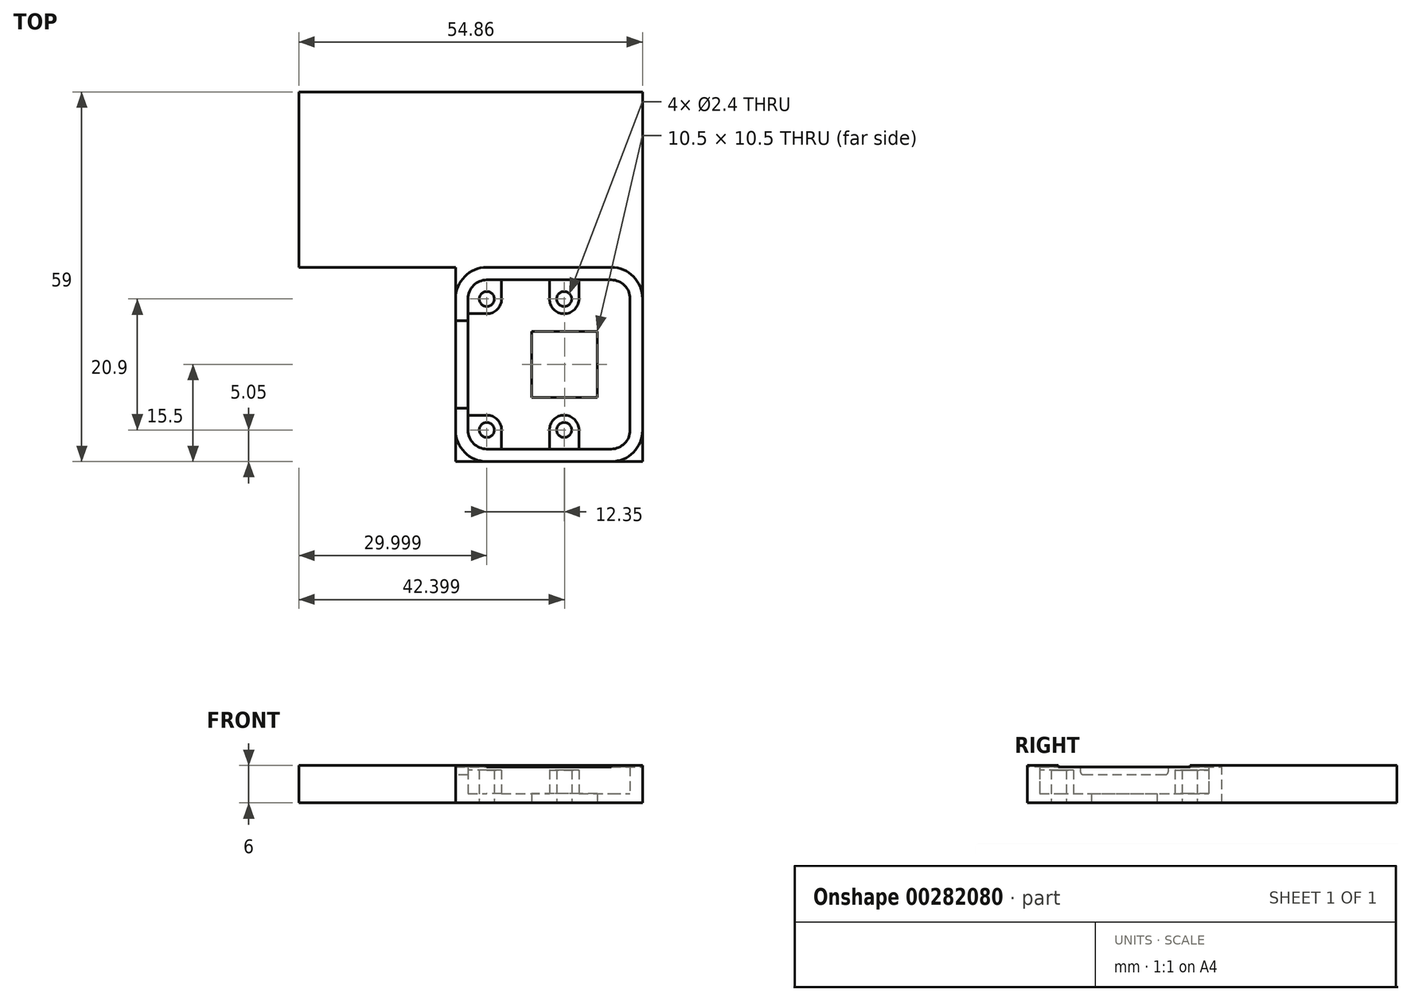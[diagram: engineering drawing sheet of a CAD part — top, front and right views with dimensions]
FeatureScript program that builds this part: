
annotation { "Feature Type Name" : "Feature", "Feature Type Description" : "" }
export const myFeature = defineFeature(function(context is Context, id is Id, definition is map)
    precondition{}
    {
        {
            var Q0;
            Q0=qCreatedBy(makeId("Top.planeOp"),FACE);
            var sketch = newSketch(context, id + "F0", { "sketchPlane" : qUnion([Q0])});
            skPoint(sketch, "E0.middle", {"position": v(0, 0) * mm});
            skPoint(sketch, "E1.visualSharp", {"position": v(-11.93, 12.5) * mm});
            skPoint(sketch, "E2.visualSharp", {"position": v(-11.93, -12.5) * mm});
            skPoint(sketch, "E3.visualSharp", {"position": v(11.93, 12.5) * mm});
            skPoint(sketch, "E4.visualSharp", {"position": v(11.93, -12.5) * mm});
            skLineSegment(sketch, "E5", {"start": v(-9.93, 14.98) * mm, "end": v(-9.93, -15.05) * mm, "construction": true});
            skLineSegment(sketch, "E6", {"start": v(-20.4, -10.45) * mm, "end": v(21.47, -10.45) * mm, "construction": true});
            skLineSegment(sketch, "E7", {"start": v(-14.71, 10.45) * mm, "end": v(19.25, 10.45) * mm, "construction": true});
            skCircle(sketch, "E8", {"center": v(-9.93, 10.45) * mm, "radius": 1.2 * mm});
            skCircle(sketch, "E9", {"center": v(-9.93, -10.45) * mm, "radius": 1.2 * mm});
            skLineSegment(sketch, "E10", {"start": v(2.42, 14.76) * mm, "end": v(2.42, -15.1) * mm, "construction": true});
            skCircle(sketch, "E11", {"center": v(2.42, 10.45) * mm, "radius": 1.2 * mm});
            skCircle(sketch, "E12", {"center": v(2.42, -10.45) * mm, "radius": 1.2 * mm});
            skLineSegment(sketch, "E13", {"start": v(2.47, 15.16) * mm, "end": v(2.47, -14.75) * mm, "construction": true});
            skLineSegment(sketch, "E14.bottom", {"start": v(6.72, -4.25) * mm, "end": v(-1.78, -4.25) * mm});
            skLineSegment(sketch, "E14.top", {"start": v(6.72, 4.25) * mm, "end": v(-1.78, 4.25) * mm});
            skLineSegment(sketch, "E14.left", {"start": v(6.72, -4.25) * mm, "end": v(6.72, 4.25) * mm});
            skLineSegment(sketch, "E14.right", {"start": v(-1.78, -4.25) * mm, "end": v(-1.78, 4.25) * mm});
            skPoint(sketch, "E14.middle", {"position": v(2.47, 0) * mm});
            skCircle(sketch, "E15", {"center": v(-9.93, 10.45) * mm, "radius": 2.35 * mm});
            skCircle(sketch, "E16", {"center": v(-9.93, -10.45) * mm, "radius": 2.35 * mm});
            skCircle(sketch, "E17", {"center": v(2.42, -10.45) * mm, "radius": 2.35 * mm});
            skCircle(sketch, "E18", {"center": v(2.42, 10.45) * mm, "radius": 2.35 * mm});
            skLineSegment(sketch, "E19.0", {"start": v(7.72, 5.25) * mm, "end": v(-2.78, 5.25) * mm});
            skLineSegment(sketch, "E19.1", {"start": v(7.72, -5.25) * mm, "end": v(7.72, 5.25) * mm});
            skLineSegment(sketch, "E19.2", {"start": v(7.72, -5.25) * mm, "end": v(-2.78, -5.25) * mm});
            skLineSegment(sketch, "E19.3", {"start": v(-2.78, -5.25) * mm, "end": v(-2.78, 5.25) * mm});
            skLineSegment(sketch, "E20.0", {"start": v(9.93, 13.5) * mm, "end": v(-9.93, 13.5) * mm});
            skArc(sketch, "E20.1", {"start": v(12.93, 10.5) * mm, "mid": v(12.05, 12.62) * mm, "end": v(9.93, 13.5) * mm});
            skArc(sketch, "E20.2", {"start": v(-9.93, 13.5) * mm, "mid": v(-12.05, 12.62) * mm, "end": v(-12.93, 10.5) * mm});
            skLineSegment(sketch, "E20.3", {"start": v(12.93, 10.5) * mm, "end": v(12.93, -10.5) * mm});
            skLineSegment(sketch, "E20.4", {"start": v(-12.93, 10.5) * mm, "end": v(-12.93, -10.5) * mm});
            skArc(sketch, "E20.5", {"start": v(-12.93, -10.5) * mm, "mid": v(-12.05, -12.62) * mm, "end": v(-9.93, -13.5) * mm});
            skLineSegment(sketch, "E20.6", {"start": v(9.93, -13.5) * mm, "end": v(-9.93, -13.5) * mm});
            skArc(sketch, "E20.7", {"start": v(9.93, -13.5) * mm, "mid": v(12.05, -12.62) * mm, "end": v(12.93, -10.5) * mm});
            skArc(sketch, "E21.0", {"start": v(14.93, 10.5) * mm, "mid": v(13.47, 14.04) * mm, "end": v(9.93, 15.5) * mm});
            skLineSegment(sketch, "E21.1", {"start": v(14.93, 10.5) * mm, "end": v(14.93, -10.5) * mm});
            skLineSegment(sketch, "E21.2", {"start": v(9.93, 15.5) * mm, "end": v(-9.93, 15.5) * mm});
            skArc(sketch, "E21.3", {"start": v(9.93, -15.5) * mm, "mid": v(13.47, -14.04) * mm, "end": v(14.93, -10.5) * mm});
            skArc(sketch, "E21.4", {"start": v(-9.93, 15.5) * mm, "mid": v(-13.47, 14.04) * mm, "end": v(-14.93, 10.5) * mm});
            skLineSegment(sketch, "E21.5", {"start": v(-14.93, 10.5) * mm, "end": v(-14.93, -10.5) * mm});
            skArc(sketch, "E21.6", {"start": v(-14.93, -10.5) * mm, "mid": v(-13.47, -14.04) * mm, "end": v(-9.93, -15.5) * mm});
            skLineSegment(sketch, "E21.7", {"start": v(9.93, -15.5) * mm, "end": v(-9.93, -15.5) * mm});
            skLineSegment(sketch, "E22", {"start": v(-9.93, 8.1) * mm, "end": v(-12.93, 8.1) * mm});
            skLineSegment(sketch, "E23", {"start": v(-7.58, 10.45) * mm, "end": v(-7.58, 13.5) * mm});
            skLineSegment(sketch, "E24", {"start": v(0.07, 10.45) * mm, "end": v(0.07, 13.5) * mm});
            skLineSegment(sketch, "E25", {"start": v(4.77, 10.45) * mm, "end": v(4.77, 13.5) * mm});
            skLineSegment(sketch, "E26", {"start": v(0.07, -10.45) * mm, "end": v(0.07, -13.5) * mm});
            skLineSegment(sketch, "E27", {"start": v(4.77, -10.45) * mm, "end": v(4.77, -13.5) * mm});
            skLineSegment(sketch, "E28", {"start": v(-9.93, -8.1) * mm, "end": v(-12.93, -8.1) * mm});
            skLineSegment(sketch, "E29", {"start": v(-7.58, -10.45) * mm, "end": v(-7.58, -13.5) * mm});
            skLineSegment(sketch, "E30", {"start": v(14.93, 10.5) * mm, "end": v(14.93, 14.98) * mm});
            skLineSegment(sketch, "E31", {"start": v(9.93, 15.5) * mm, "end": v(14.93, 15.5) * mm});
            skLineSegment(sketch, "E32", {"start": v(14.93, 15.5) * mm, "end": v(14.93, 14.98) * mm});
            skLineSegment(sketch, "E33", {"start": v(9.93, -15.5) * mm, "end": v(14.93, -15.5) * mm});
            skLineSegment(sketch, "E34", {"start": v(14.93, -15.5) * mm, "end": v(14.93, -10.5) * mm});
            skLineSegment(sketch, "E35", {"start": v(-14.93, 10.5) * mm, "end": v(-14.93, 15.5) * mm});
            skLineSegment(sketch, "E36", {"start": v(-14.93, 15.5) * mm, "end": v(-9.93, 15.5) * mm});
            skLineSegment(sketch, "E37", {"start": v(-14.93, -10.5) * mm, "end": v(-14.93, -15.5) * mm});
            skLineSegment(sketch, "E38", {"start": v(-14.93, -15.5) * mm, "end": v(-9.93, -15.5) * mm});
            skLineSegment(sketch, "E39.left", {"start": v(-14.93, 15.5) * mm, "end": v(-14.93, -15.5) * mm});
            skLineSegment(sketch, "E40.left", {"start": v(14.93, 15.5) * mm, "end": v(14.93, -15.5) * mm});
            skLineSegment(sketch, "E41", {"start": v(-14.93, 15.5) * mm, "end": v(-14.93, 43.5) * mm});
            skLineSegment(sketch, "E42", {"start": v(-14.93, 43.5) * mm, "end": v(14.93, 43.5) * mm});
            skLineSegment(sketch, "E43", {"start": v(14.93, 43.5) * mm, "end": v(14.93, 15.5) * mm});
            skLineSegment(sketch, "E44", {"start": v(-14.93, 15.5) * mm, "end": v(-39.93, 15.5) * mm});
            skLineSegment(sketch, "E45", {"start": v(-39.93, 15.5) * mm, "end": v(-39.93, 43.5) * mm});
            skLineSegment(sketch, "E46", {"start": v(-39.93, 43.5) * mm, "end": v(-14.93, 43.5) * mm});
            skSolve(sketch);
        }
        {
            var Q0;
            Q0=makeQuery(id+"F0.imprint","IMPRINT",FACE,{"disambiguationData":[TD([[makeQuery(id+"F0.imprint","IMPRINT",EDGE,{"derivedFrom":sQuery(id+"F0.wireOp",EDGE,"E20.0")}),-1.0]])]});
            var Q1;
            Q1=makeQuery(id+"F0.imprint","IMPRINT",FACE,{"disambiguationData":[TD([[makeQuery(id+"F0.imprint","IMPRINT",EDGE,{"derivedFrom":sQuery(id+"F0.wireOp",EDGE,"E0.left")}),-1.0]])]});
            var Q2;
            Q2=makeQuery(id+"F0.imprint","IMPRINT",FACE,{"disambiguationData":[TD([[makeQuery(id+"F0.imprint","IMPRINT",EDGE,{"derivedFrom":sQuery(id+"F0.wireOp",EDGE,"E12")}),-1.0]])]});
            var Q3;
            {var subQ0=sQuery(id+"F0.wireOp",EDGE,"E2.filletArc");Q3=makeQuery(id+"F0.imprint","IMPRINT",FACE,{"disambiguationData":[TD([[makeQuery(id+"F0.imprint","IMPRINT",EDGE,{"derivedFrom":subQ0}),1.0]])]});}
            var Q4;
            Q4=makeQuery(id+"F0.imprint","IMPRINT",FACE,{"disambiguationData":[TD([[makeQuery(id+"F0.imprint","IMPRINT",EDGE,{"derivedFrom":sQuery(id+"F0.wireOp",EDGE,"E0.left")}),1.0]])]});
            var Q5;
            {var subQ0=sQuery(id+"F0.wireOp",EDGE,"E1.filletArc");Q5=makeQuery(id+"F0.imprint","IMPRINT",FACE,{"disambiguationData":[TD([[makeQuery(id+"F0.imprint","IMPRINT",EDGE,{"derivedFrom":subQ0}),1.0]])]});}
            var Q6;
            Q6=makeQuery(id+"F0.imprint","IMPRINT",FACE,{"disambiguationData":[TD([[makeQuery(id+"F0.imprint","IMPRINT",EDGE,{"derivedFrom":sQuery(id+"F0.wireOp",EDGE,"E11")}),-1.0]])]});
            var Q7;
            {var subQ0=sQuery(id+"F0.wireOp",EDGE,"E18");var subQ1=sQuery(id+"F0.wireOp",EDGE,"E0.bottom");var subQ2=makeQuery(id+"F0.imprint","INTERSECT",VERTEX,{"disambiguationData":[OD(0.0)],"derivedFrom":[subQ1,subQ0]});Q7=makeQuery(id+"F0.imprint","IMPRINT",FACE,{"disambiguationData":[TD([[makeQuery(id+"F0.imprint","IMPRINT",EDGE,{"disambiguationData":[TD([[subQ2,-1.0]])],"derivedFrom":subQ1}),-1.0]])]});}
            var Q8;
            {var subQ0=sQuery(id+"F0.wireOp",EDGE,"E1.filletArc");Q8=makeQuery(id+"F0.imprint","IMPRINT",FACE,{"disambiguationData":[TD([[makeQuery(id+"F0.imprint","IMPRINT",EDGE,{"derivedFrom":subQ0}),-1.0]])]});}
            var Q9;
            {var subQ0=sQuery(id+"F0.wireOp",EDGE,"E2.filletArc");Q9=makeQuery(id+"F0.imprint","IMPRINT",FACE,{"disambiguationData":[TD([[makeQuery(id+"F0.imprint","IMPRINT",EDGE,{"derivedFrom":subQ0}),-1.0]])]});}
            var Q10;
            {var subQ0=sQuery(id+"F0.wireOp",EDGE,"E17");var subQ1=sQuery(id+"F0.wireOp",EDGE,"E0.top");var subQ2=makeQuery(id+"F0.imprint","INTERSECT",VERTEX,{"disambiguationData":[OD(0.0)],"derivedFrom":[subQ1,subQ0]});Q10=makeQuery(id+"F0.imprint","IMPRINT",FACE,{"disambiguationData":[TD([[makeQuery(id+"F0.imprint","IMPRINT",EDGE,{"disambiguationData":[TD([[subQ2,-1.0]])],"derivedFrom":subQ1}),1.0]])]});}
            var Q11;
            {var subQ0=sQuery(id+"F0.wireOp",EDGE,"E20.2");Q11=makeQuery(id+"F0.imprint","IMPRINT",FACE,{"disambiguationData":[TD([[makeQuery(id+"F0.imprint","IMPRINT",EDGE,{"derivedFrom":subQ0}),1.0]])]});}
            var Q12;
            {var subQ0=sQuery(id+"F0.wireOp",EDGE,"E22");var subQ1=sQuery(id+"F0.wireOp",EDGE,"E0.right");var subQ2=makeQuery(id+"F0.imprint","INTERSECT",VERTEX,{"derivedFrom":[subQ1,subQ0]});Q12=makeQuery(id+"F0.imprint","IMPRINT",FACE,{"disambiguationData":[TD([[makeQuery(id+"F0.imprint","IMPRINT",EDGE,{"disambiguationData":[TD([[subQ2,-1.0]])],"derivedFrom":subQ1}),-1.0]])]});}
            var Q13;
            {var subQ0=sQuery(id+"F0.wireOp",EDGE,"E20.5");Q13=makeQuery(id+"F0.imprint","IMPRINT",FACE,{"disambiguationData":[TD([[makeQuery(id+"F0.imprint","IMPRINT",EDGE,{"derivedFrom":subQ0}),1.0]])]});}
            var Q14;
            {var subQ0=sQuery(id+"F0.wireOp",EDGE,"E28");var subQ1=sQuery(id+"F0.wireOp",EDGE,"E0.right");var subQ2=makeQuery(id+"F0.imprint","INTERSECT",VERTEX,{"derivedFrom":[subQ1,subQ0]});Q14=makeQuery(id+"F0.imprint","IMPRINT",FACE,{"disambiguationData":[TD([[makeQuery(id+"F0.imprint","IMPRINT",EDGE,{"disambiguationData":[TD([[subQ2,-1.0]])],"derivedFrom":subQ1}),1.0]])]});}
            var Q15;
            {var subQ0=sQuery(id+"F0.wireOp",EDGE,"E29");var subQ1=sQuery(id+"F0.wireOp",EDGE,"E0.top");var subQ2=makeQuery(id+"F0.imprint","INTERSECT",VERTEX,{"derivedFrom":[subQ1,subQ0]});Q15=makeQuery(id+"F0.imprint","IMPRINT",FACE,{"disambiguationData":[TD([[makeQuery(id+"F0.imprint","IMPRINT",EDGE,{"disambiguationData":[TD([[subQ2,-1.0]])],"derivedFrom":subQ1}),-1.0]])]});}
            var Q16;
            {var subQ0=sQuery(id+"F0.wireOp",EDGE,"E26");var subQ1=sQuery(id+"F0.wireOp",EDGE,"E0.top");var subQ2=makeQuery(id+"F0.imprint","INTERSECT",VERTEX,{"derivedFrom":[subQ1,subQ0]});Q16=makeQuery(id+"F0.imprint","IMPRINT",FACE,{"disambiguationData":[TD([[makeQuery(id+"F0.imprint","IMPRINT",EDGE,{"disambiguationData":[TD([[subQ2,-1.0]])],"derivedFrom":subQ1}),1.0]])]});}
            var Q17;
            {var subQ3=sQuery(id+"F0.wireOp",EDGE,"E27");var subQ6=sQuery(id+"F0.wireOp",EDGE,"E0.top");var subQ10=makeQuery(id+"F0.imprint","INTERSECT",VERTEX,{"derivedFrom":[subQ6,subQ3]});Q17=makeQuery(id+"F0.imprint","IMPRINT",FACE,{"disambiguationData":[TD([[makeQuery(id+"F0.imprint","IMPRINT",EDGE,{"disambiguationData":[TD([[subQ10,-1.0]])],"derivedFrom":subQ6}),1.0]])]});}
            var Q18;
            {var subQ0=sQuery(id+"F0.wireOp",EDGE,"E27");var subQ1=sQuery(id+"F0.wireOp",EDGE,"E0.top");var subQ2=makeQuery(id+"F0.imprint","INTERSECT",VERTEX,{"derivedFrom":[subQ1,subQ0]});Q18=makeQuery(id+"F0.imprint","IMPRINT",FACE,{"disambiguationData":[TD([[makeQuery(id+"F0.imprint","IMPRINT",EDGE,{"disambiguationData":[TD([[subQ2,-1.0]])],"derivedFrom":subQ1}),-1.0]])]});}
            var Q19;
            {var subQ0=sQuery(id+"F0.wireOp",EDGE,"E17");var subQ1=sQuery(id+"F0.wireOp",EDGE,"E0.top");var subQ2=makeQuery(id+"F0.imprint","INTERSECT",VERTEX,{"disambiguationData":[OD(1.0)],"derivedFrom":[subQ1,subQ0]});Q19=makeQuery(id+"F0.imprint","IMPRINT",FACE,{"disambiguationData":[TD([[makeQuery(id+"F0.imprint","IMPRINT",EDGE,{"disambiguationData":[TD([[subQ2,-1.0]])],"derivedFrom":subQ1}),-1.0]])]});}
            var Q20;
            {var subQ0=sQuery(id+"F0.wireOp",EDGE,"E23");var subQ1=sQuery(id+"F0.wireOp",EDGE,"E0.bottom");var subQ2=makeQuery(id+"F0.imprint","INTERSECT",VERTEX,{"derivedFrom":[subQ1,subQ0]});Q20=makeQuery(id+"F0.imprint","IMPRINT",FACE,{"disambiguationData":[TD([[makeQuery(id+"F0.imprint","IMPRINT",EDGE,{"disambiguationData":[TD([[subQ2,-1.0]])],"derivedFrom":subQ1}),1.0]])]});}
            var Q21;
            {var subQ0=sQuery(id+"F0.wireOp",EDGE,"E15");var subQ1=sQuery(id+"F0.wireOp",EDGE,"E0.right");var subQ2=makeQuery(id+"F0.imprint","INTERSECT",VERTEX,{"derivedFrom":[subQ1,subQ0]});Q21=makeQuery(id+"F0.imprint","IMPRINT",FACE,{"disambiguationData":[TD([[makeQuery(id+"F0.imprint","IMPRINT",EDGE,{"disambiguationData":[TD([[subQ2,-1.0]])],"derivedFrom":subQ1}),1.0]])]});}
            var Q22;
            {var subQ0=sQuery(id+"F0.wireOp",EDGE,"E24");var subQ1=sQuery(id+"F0.wireOp",EDGE,"E0.bottom");var subQ2=makeQuery(id+"F0.imprint","INTERSECT",VERTEX,{"derivedFrom":[subQ1,subQ0]});Q22=makeQuery(id+"F0.imprint","IMPRINT",FACE,{"disambiguationData":[TD([[makeQuery(id+"F0.imprint","IMPRINT",EDGE,{"disambiguationData":[TD([[subQ2,-1.0]])],"derivedFrom":subQ1}),-1.0]])]});}
            var Q23;
            {var subQ0=sQuery(id+"F0.wireOp",EDGE,"E18");var subQ1=sQuery(id+"F0.wireOp",EDGE,"E0.bottom");var subQ2=makeQuery(id+"F0.imprint","INTERSECT",VERTEX,{"disambiguationData":[OD(1.0)],"derivedFrom":[subQ1,subQ0]});Q23=makeQuery(id+"F0.imprint","IMPRINT",FACE,{"disambiguationData":[TD([[makeQuery(id+"F0.imprint","IMPRINT",EDGE,{"disambiguationData":[TD([[subQ2,-1.0]])],"derivedFrom":subQ1}),1.0]])]});}
            var Q24;
            {var subQ1=sQuery(id+"F0.wireOp",EDGE,"E0.bottom");var subQ7=sQuery(id+"F0.wireOp",EDGE,"E25");var subQ9=makeQuery(id+"F0.imprint","INTERSECT",VERTEX,{"derivedFrom":[subQ1,subQ7]});Q24=makeQuery(id+"F0.imprint","IMPRINT",FACE,{"disambiguationData":[TD([[makeQuery(id+"F0.imprint","IMPRINT",EDGE,{"disambiguationData":[TD([[subQ9,-1.0]])],"derivedFrom":subQ1}),-1.0]])]});}
            var Q25;
            {var subQ0=sQuery(id+"F0.wireOp",EDGE,"E25");var subQ1=sQuery(id+"F0.wireOp",EDGE,"E0.bottom");var subQ2=makeQuery(id+"F0.imprint","INTERSECT",VERTEX,{"derivedFrom":[subQ1,subQ0]});Q25=makeQuery(id+"F0.imprint","IMPRINT",FACE,{"disambiguationData":[TD([[makeQuery(id+"F0.imprint","IMPRINT",EDGE,{"disambiguationData":[TD([[subQ2,-1.0]])],"derivedFrom":subQ1}),1.0]])]});}
            var Q26;
            Q26=makeQuery(id+"F0.imprint","IMPRINT",FACE,{"disambiguationData":[TD([[makeQuery(id+"F0.imprint","IMPRINT",EDGE,{"derivedFrom":sQuery(id+"F0.wireOp",EDGE,"E19.0")}),-1.0]])]});
            var Q27;
            Q27=makeQuery(id+"F0.imprint","IMPRINT",FACE,{"disambiguationData":[TD([[makeQuery(id+"F0.imprint","IMPRINT",EDGE,{"derivedFrom":sQuery(id+"F0.wireOp",EDGE,"E9")}),-1.0]])]});
            var Q28;
            {var subQ0=sQuery(id+"F0.wireOp",EDGE,"E26");Q28=makeQuery(id+"F0.imprint","IMPRINT",FACE,{"disambiguationData":[TD([[makeQuery(id+"F0.imprint","IMPRINT",EDGE,{"derivedFrom":subQ0}),1.0]])]});}
            var Q29;
            Q29=makeQuery(id+"F0.imprint","IMPRINT",FACE,{"disambiguationData":[TD([[makeQuery(id+"F0.imprint","IMPRINT",EDGE,{"derivedFrom":sQuery(id+"F0.wireOp",EDGE,"E8")}),-1.0]])]});
            var Q30;
            {var subQ0=sQuery(id+"F0.wireOp",EDGE,"E24");Q30=makeQuery(id+"F0.imprint","IMPRINT",FACE,{"disambiguationData":[TD([[makeQuery(id+"F0.imprint","IMPRINT",EDGE,{"derivedFrom":subQ0}),-1.0]])]});}
            extrude(context, id + "F1", {"entities" : qUnion([Q0, Q1, Q2, Q3, Q4, Q5, Q6, Q7, Q8, Q9, Q10, Q11, Q12, Q13, Q14, Q15, Q16, Q17, Q18, Q19, Q20, Q21, Q22, Q23, Q24, Q25, Q26, Q27, Q28, Q29, Q30]), "depth" : 1.5 * mm});
        }
        {
            var Q0;
            {var subQ1=sQuery(id+"F0.wireOp",EDGE,"E20.2");Q0=makeQuery(id+"F0.imprint","IMPRINT",FACE,{"disambiguationData":[TD([[makeQuery(id+"F0.imprint","IMPRINT",EDGE,{"derivedFrom":subQ1}),1.0]])]});}
            var Q1;
            Q1=makeQuery(id+"F0.imprint","IMPRINT",FACE,{"disambiguationData":[TD([[makeQuery(id+"F0.imprint","IMPRINT",EDGE,{"derivedFrom":sQuery(id+"F0.wireOp",EDGE,"E8")}),-1.0]])]});
            var Q2;
            Q2=makeQuery(id+"F0.imprint","IMPRINT",FACE,{"disambiguationData":[TD([[makeQuery(id+"F0.imprint","IMPRINT",EDGE,{"derivedFrom":sQuery(id+"F0.wireOp",EDGE,"E11")}),-1.0]])]});
            var Q3;
            {var subQ0=sQuery(id+"F0.wireOp",EDGE,"E24");Q3=makeQuery(id+"F0.imprint","IMPRINT",FACE,{"disambiguationData":[TD([[makeQuery(id+"F0.imprint","IMPRINT",EDGE,{"derivedFrom":subQ0}),-1.0]])]});}
            var Q4;
            Q4=makeQuery(id+"F0.imprint","IMPRINT",FACE,{"disambiguationData":[TD([[makeQuery(id+"F0.imprint","IMPRINT",EDGE,{"derivedFrom":sQuery(id+"F0.wireOp",EDGE,"E12")}),-1.0]])]});
            var Q5;
            {var subQ0=sQuery(id+"F0.wireOp",EDGE,"E26");Q5=makeQuery(id+"F0.imprint","IMPRINT",FACE,{"disambiguationData":[TD([[makeQuery(id+"F0.imprint","IMPRINT",EDGE,{"derivedFrom":subQ0}),1.0]])]});}
            var Q6;
            Q6=makeQuery(id+"F0.imprint","IMPRINT",FACE,{"disambiguationData":[TD([[makeQuery(id+"F0.imprint","IMPRINT",EDGE,{"derivedFrom":sQuery(id+"F0.wireOp",EDGE,"E9")}),-1.0]])]});
            var Q7;
            {var subQ1=sQuery(id+"F0.wireOp",EDGE,"E20.5");Q7=makeQuery(id+"F0.imprint","IMPRINT",FACE,{"disambiguationData":[TD([[makeQuery(id+"F0.imprint","IMPRINT",EDGE,{"derivedFrom":subQ1}),1.0]])]});}
            extrude(context, id + "F2", {"entities" : qUnion([Q0, Q1, Q2, Q3, Q4, Q5, Q6, Q7]), "operationType" : NewBodyOperationType.ADD, "depth" : 5.25 * mm});
        }
        {
            var Q0;
            {var subQ12=sQuery(id+"F0.wireOp",EDGE,"E20.1");Q0=makeQuery(id+"F0.imprint","IMPRINT",FACE,{"disambiguationData":[TD([[makeQuery(id+"F0.imprint","IMPRINT",EDGE,{"derivedFrom":subQ12}),-1.0]])]});}
            extrude(context, id + "F3", {"entities" : qUnion([Q0]), "operationType" : NewBodyOperationType.ADD, "depth" : 5.75 * mm});
        }
        {
            var Q0;
            {var subQ0=sQuery(id+"F0.wireOp",EDGE,"E21.5");Q0=makeQuery(id+"F3.boolean.opBoolean","MERGE",FACE,{"derivedFrom":[makeQuery(id+"F1.opExtrude","SWEPT_FACE",FACE,{"disambiguationData":[OSD([subQ0])]}),makeQuery(id+"F3.opExtrude","SWEPT_FACE",FACE,{"disambiguationData":[OSD([subQ0])]})]});}
            var sketch = newSketch(context, id + "F4", { "sketchPlane" : qUnion([Q0])});
            skLineSegment(sketch, "E47.bottom", {"start": v(-7, 5.75) * mm, "end": v(7, 5.75) * mm});
            skLineSegment(sketch, "E47.top", {"start": v(-6.5, 4.5) * mm, "end": v(6.5, 4.5) * mm});
            skLineSegment(sketch, "E47.left", {"start": v(-7, 5.75) * mm, "end": v(-7, 5) * mm});
            skLineSegment(sketch, "E47.right", {"start": v(7, 5.75) * mm, "end": v(7, 5) * mm});
            skPoint(sketch, "E48.visualSharp", {"position": v(-7, 4.5) * mm});
            skArc(sketch, "E48.filletArc", {"start": v(-7, 5) * mm, "mid": v(-6.85, 4.65) * mm, "end": v(-6.5, 4.5) * mm});
            skPoint(sketch, "E49.visualSharp", {"position": v(7, 4.5) * mm});
            skArc(sketch, "E49.filletArc", {"start": v(6.5, 4.5) * mm, "mid": v(6.85, 4.65) * mm, "end": v(7, 5) * mm});
            skSolve(sketch);
        }
        {
            var Q0;
            Q0=makeQuery(id+"F4.imprint","IMPRINT",FACE,{"disambiguationData":[TD([[makeQuery(id+"F4.imprint","IMPRINT",EDGE,{"derivedFrom":sQuery(id+"F4.wireOp",EDGE,"E47.bottom")}),-1.0]])]});
            extrude(context, id + "F5", {"entities" : qUnion([Q0]), "operationType" : NewBodyOperationType.REMOVE, "oppositeDirection" : true, "depth" : 2 * mm});
        }
        {
            var Q0;
            {var subQ0=sQuery(id+"F0.wireOp",EDGE,"E21.4");Q0=makeQuery(id+"F0.imprint","IMPRINT",FACE,{"disambiguationData":[TD([[makeQuery(id+"F0.imprint","IMPRINT",EDGE,{"derivedFrom":subQ0}),-1.0]])]});}
            var Q1;
            {var subQ3=sQuery(id+"F0.wireOp",EDGE,"E39.bottom");Q1=makeQuery(id+"F0.imprint","IMPRINT",FACE,{"disambiguationData":[TD([[makeQuery(id+"F0.imprint","IMPRINT",EDGE,{"derivedFrom":subQ3}),1.0]])]});}
            var Q2;
            {var subQ0=sQuery(id+"F0.wireOp",EDGE,"E21.3");Q2=makeQuery(id+"F0.imprint","IMPRINT",FACE,{"disambiguationData":[TD([[makeQuery(id+"F0.imprint","IMPRINT",EDGE,{"derivedFrom":subQ0}),-1.0]])]});}
            var Q3;
            {var subQ0=sQuery(id+"F0.wireOp",EDGE,"E21.0");Q3=makeQuery(id+"F0.imprint","IMPRINT",FACE,{"disambiguationData":[TD([[makeQuery(id+"F0.imprint","IMPRINT",EDGE,{"derivedFrom":subQ0}),-1.0]])]});}
            var Q4;
            {var subQ3=sQuery(id+"F0.wireOp",EDGE,"E40.bottom");Q4=makeQuery(id+"F0.imprint","IMPRINT",FACE,{"disambiguationData":[TD([[makeQuery(id+"F0.imprint","IMPRINT",EDGE,{"derivedFrom":subQ3}),-1.0]])]});}
            var Q5;
            {var subQ0=sQuery(id+"F0.wireOp",EDGE,"E21.6");Q5=makeQuery(id+"F0.imprint","IMPRINT",FACE,{"disambiguationData":[TD([[makeQuery(id+"F0.imprint","IMPRINT",EDGE,{"derivedFrom":subQ0}),-1.0]])]});}
            extrude(context, id + "F6", {"entities" : qUnion([Q0, Q1, Q2, Q3, Q4, Q5]), "operationType" : NewBodyOperationType.ADD, "depth" : 6 * mm});
        }
        {
            var Q0;
            Q0=makeQuery(id+"F0.imprint","IMPRINT",FACE,{"disambiguationData":[TD([[makeQuery(id+"F0.imprint","IMPRINT",EDGE,{"derivedFrom":sQuery(id+"F0.wireOp",EDGE,"E21.7")}),1.0]])]});
            var Q1;
            Q1=makeQuery(id+"F0.imprint","IMPRINT",FACE,{"disambiguationData":[TD([[makeQuery(id+"F0.imprint","IMPRINT",EDGE,{"derivedFrom":sQuery(id+"F0.wireOp",EDGE,"m4zwP7YD-bymP-fUut-T2Se-XZHOzdcVZs3e")}),-1.0]])]});
            var Q2;
            Q2=makeQuery(id+"F0.imprint","IMPRINT",FACE,{"disambiguationData":[TD([[makeQuery(id+"F0.imprint","IMPRINT",EDGE,{"derivedFrom":sQuery(id+"F0.wireOp",EDGE,"E41")}),1.0]])]});
            var Q3;
            Q3=makeQuery(id+"F0.imprint","IMPRINT",FACE,{"disambiguationData":[TD([[makeQuery(id+"F0.imprint","IMPRINT",EDGE,{"derivedFrom":sQuery(id+"F0.wireOp",EDGE,"E21.2")}),-1.0]])]});
            extrude(context, id + "F7", {"entities" : qUnion([Q0, Q1, Q2, Q3]), "operationType" : NewBodyOperationType.ADD, "depth" : 6 * mm});
        }
    });
